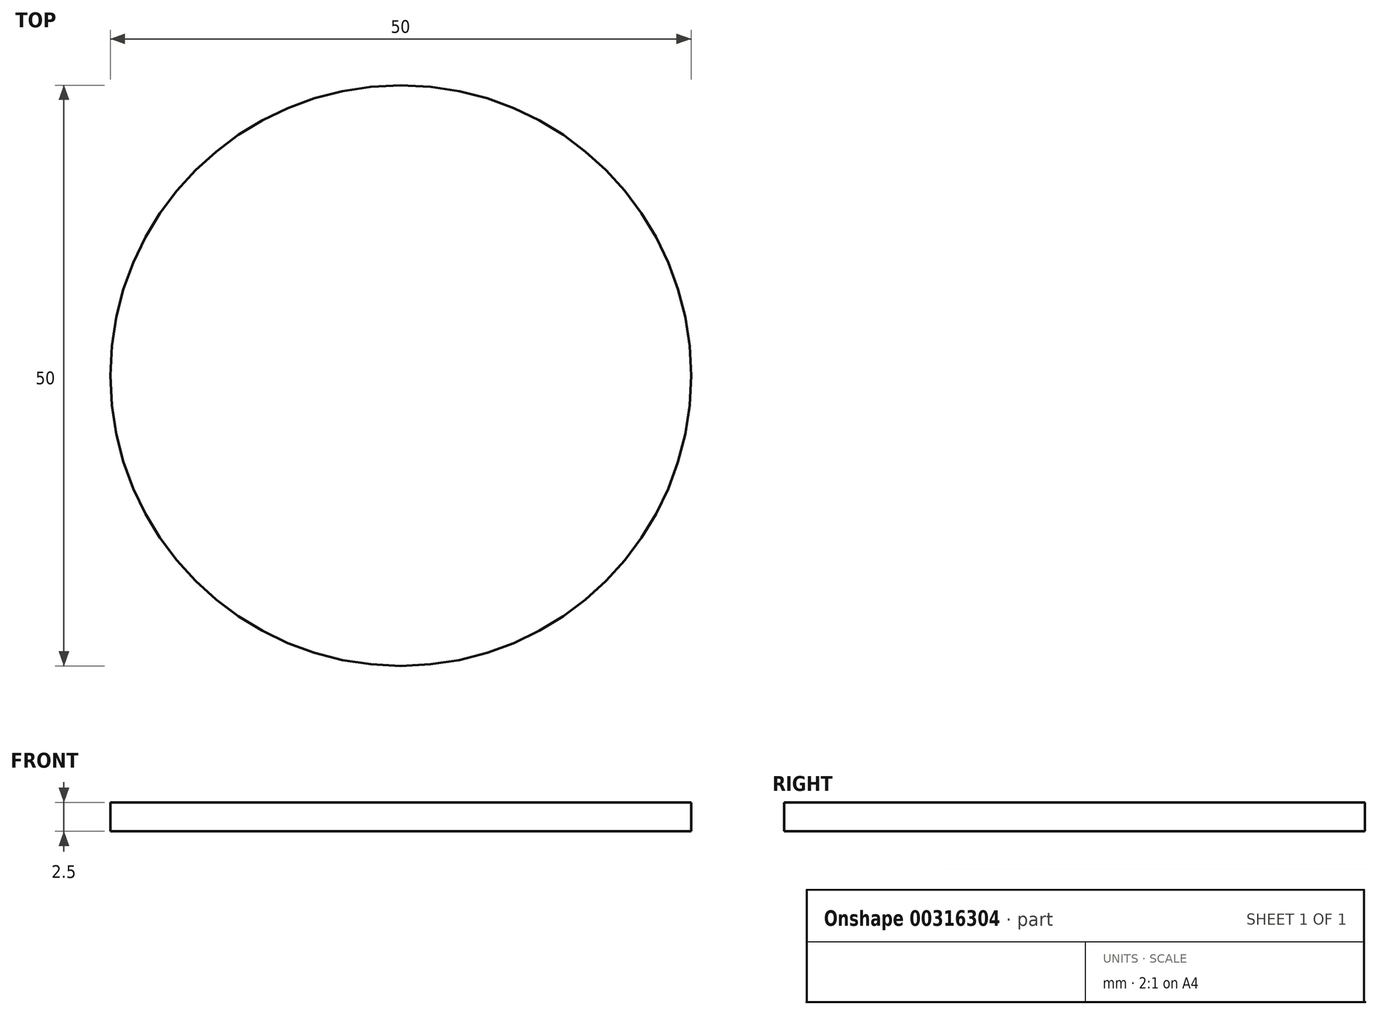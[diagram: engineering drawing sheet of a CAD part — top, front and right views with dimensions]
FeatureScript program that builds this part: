
annotation { "Feature Type Name" : "Feature", "Feature Type Description" : "" }
export const myFeature = defineFeature(function(context is Context, id is Id, definition is map)
    precondition{}
    {
        {
            var Q0;
            Q0=qCreatedBy(makeId("Top.planeOp"),FACE);
            var sketch = newSketch(context, id + "F0", { "sketchPlane" : qUnion([Q0])});
            skCircle(sketch, "E0", {"center": v(0, 0) * mm, "radius": 25 * mm});
            skSolve(sketch);
        }
        {
            var Q0;
            Q0 = qSketchRegion(id + "F0", true);
            extrude(context, id + "F1", {"entities" : qUnion([Q0]), "depth" : 2.5 * mm});
        }
    });
